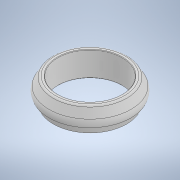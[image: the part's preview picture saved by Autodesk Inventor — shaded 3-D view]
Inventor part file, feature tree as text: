
AUTODESK INVENTOR PART (.ipt)
format: ipt  version: 2020 (Build 240168000, 168)  size: 154,624 bytes
history: native  units: mm
features: revolve x1, chamfer x1, sketch x1
ambient origin geometry x8: Origin, YZ Plane, XZ Plane, XY Plane, X Axis, Y Axis, Z Axis, Center Point
bodies: Solid1 (feature_tree)
feature tree (3):
  revolve  "Revolution1"  [1 undecoded]
  chamfer  "Chamfer1"  Distance=0.8mm
  sketch  "Sketch1"  dims[d0=5.0mm d1=6.45mm d2=0.8mm d3=1.5mm d4=0.5mm d5=2.0mm d6=90.0deg d7=0.1mm d8=2.0mm d9=45.0deg]
note: 1 required parameter value undecoded (feature->parameter linkage not recoverable at this tier; creation-order binding heuristic only, values carry confidence <= 0.55)
